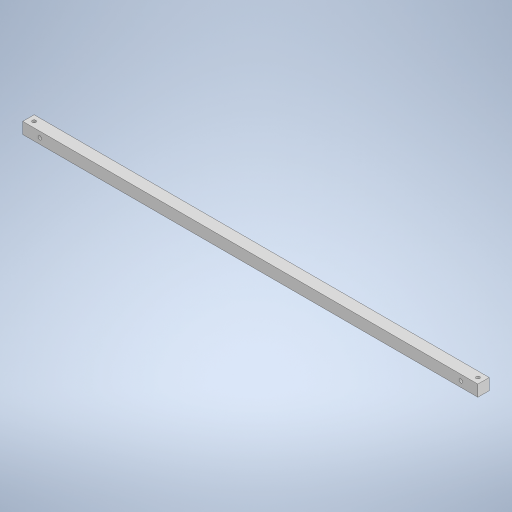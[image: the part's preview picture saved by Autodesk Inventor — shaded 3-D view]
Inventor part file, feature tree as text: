
AUTODESK INVENTOR PART (.ipt)
format: ipt  version: 2023 (Build 270158000, 158)  size: 251,392 bytes
history: native  units: mm
features: sketch x3, hole x2, other x1, extrude x1
ambient origin geometry x8: Origin, YZ Plane, XZ Plane, XY Plane, X Axis, Y Axis, Z Axis, Center Point
bodies: Body1 (feature_tree)
feature tree (7):
  other  "ソリッド1"
  extrude  "押し出し1"  Depth=400.0mm
  hole  "穴1"  [1 undecoded]
  hole  "穴2"  [1 undecoded]
  sketch  "スケッチ1"
  sketch  "スケッチ4"
  sketch  "スケッチ5"
note: 2 required parameter values undecoded (feature->parameter linkage not recoverable at this tier; creation-order binding heuristic only, values carry confidence <= 0.55)
